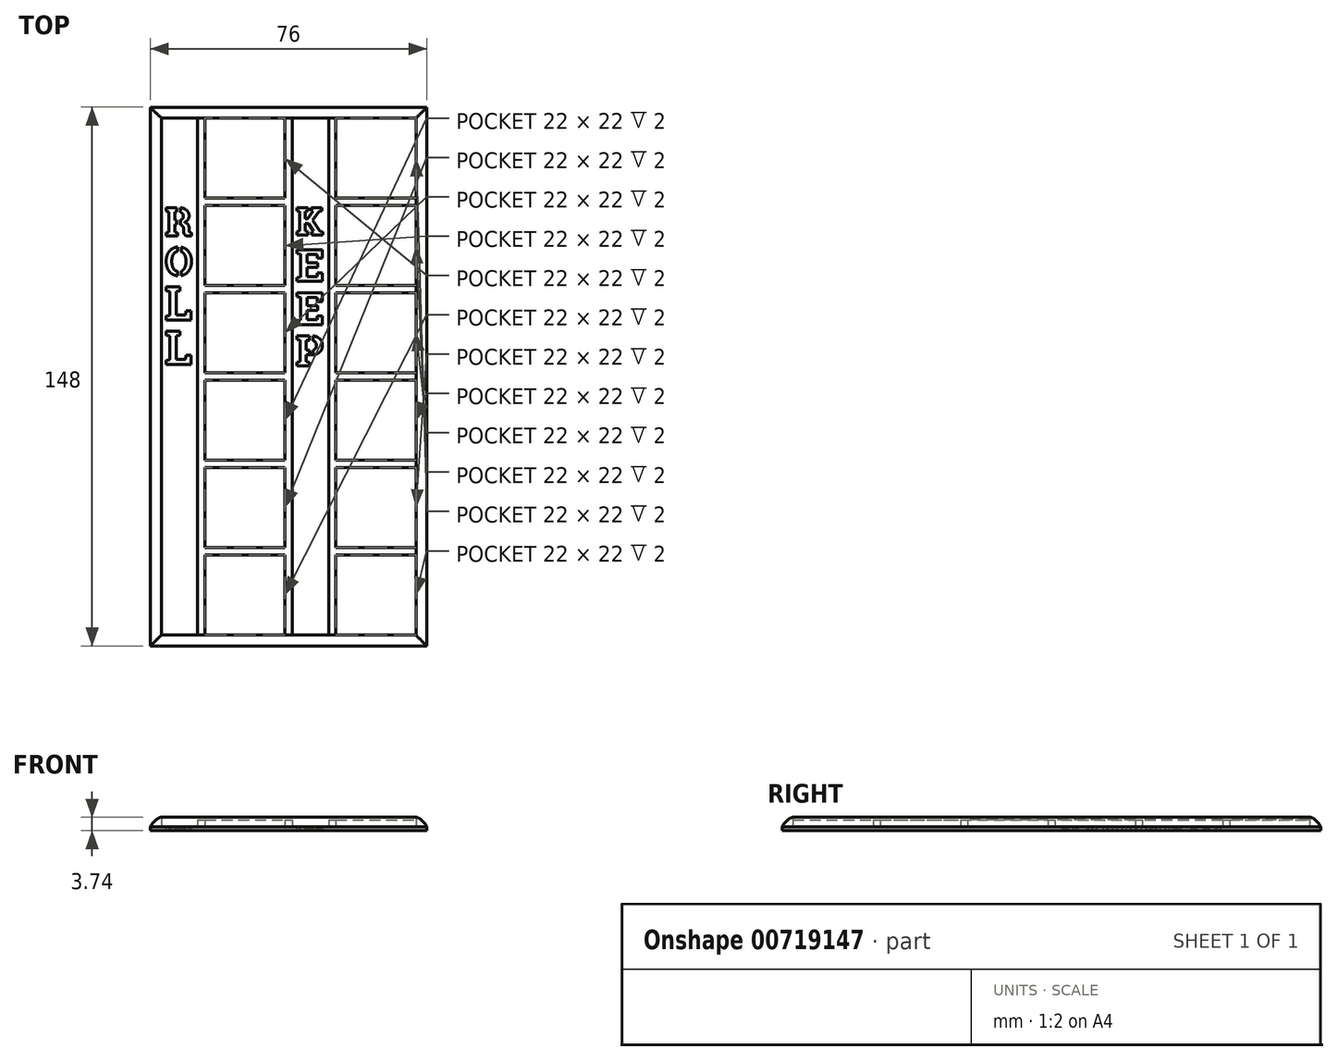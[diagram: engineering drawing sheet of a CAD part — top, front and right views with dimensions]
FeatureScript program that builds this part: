
annotation { "Feature Type Name" : "Feature", "Feature Type Description" : "" }
export const myFeature = defineFeature(function(context is Context, id is Id, definition is map)
    precondition{}
    {
        {
            var Q0;
            Q0=qCreatedBy(makeId("Top.planeOp"),FACE);
            var sketch = newSketch(context, id + "F0", { "sketchPlane" : qUnion([Q0])});
            skLineSegment(sketch, "E0.bottom", {"start": v(-38, 75.1) * mm, "end": v(38, 75.1) * mm});
            skLineSegment(sketch, "E0.top", {"start": v(-38, -72.9) * mm, "end": v(38, -72.9) * mm});
            skLineSegment(sketch, "E0.left", {"start": v(-38, 75.1) * mm, "end": v(-38, -72.9) * mm});
            skLineSegment(sketch, "E0.right", {"start": v(38, 75.1) * mm, "end": v(38, -72.9) * mm});
            skLineSegment(sketch, "E1.left", {"start": v(11, -69.9) * mm, "end": v(11, 72.1) * mm});
            skLineSegment(sketch, "E1.right", {"start": v(-35, -69.9) * mm, "end": v(-35, 72.1) * mm});
            skLineSegment(sketch, "E2", {"start": v(-25, 72.1) * mm, "end": v(-25, -69.9) * mm});
            skLineSegment(sketch, "E3.1.0.0", {"start": v(-1, 72.1) * mm, "end": v(-1, -69.9) * mm});
            skLineSegment(sketch, "E3.2.0.0", {"start": v(13, 72.1) * mm, "end": v(13, -69.9) * mm});
            skLineSegment(sketch, "E4", {"start": v(-23, -69.9) * mm, "end": v(-23, 72.1) * mm});
            skLineSegment(sketch, "E5.1.0.0", {"start": v(1, -69.9) * mm, "end": v(1, 72.1) * mm});
            skLineSegment(sketch, "E5.2.0.0", {"start": v(35, -69.9) * mm, "end": v(35, 72.1) * mm});
            skLineSegment(sketch, "E6", {"start": v(-35, 72.1) * mm, "end": v(35, 72.1) * mm});
            skLineSegment(sketch, "E7", {"start": v(35, -69.9) * mm, "end": v(-35, -69.9) * mm});
            skLineSegment(sketch, "E8.bottom", {"start": v(-29.5, 28.1) * mm, "end": v(-30.5, 28.1) * mm});
            skLineSegment(sketch, "E8.top", {"start": v(-29.5, 38.1) * mm, "end": v(-30.5, 38.1) * mm});
            skLineSegment(sketch, "E8.left", {"start": v(-29.5, 28.1) * mm, "end": v(-29.5, 38.1) * mm});
            skLineSegment(sketch, "E8.right", {"start": v(-30.5, 28.1) * mm, "end": v(-30.5, 38.1) * mm});
            skLineSegment(sketch, "E9.bottom", {"start": v(-30.75, 48.1) * mm, "end": v(-29.75, 48.1) * mm});
            skLineSegment(sketch, "E9.top", {"start": v(-30.75, 42.1) * mm, "end": v(-29.75, 42.1) * mm});
            skLineSegment(sketch, "E9.left", {"start": v(-30.75, 48.1) * mm, "end": v(-30.75, 42.1) * mm});
            skLineSegment(sketch, "E9.right", {"start": v(-29.75, 48.1) * mm, "end": v(-29.75, 42.1) * mm});
            skLineSegment(sketch, "E10.bottom", {"start": v(5.75, 7.6) * mm, "end": v(6.75, 7.6) * mm});
            skLineSegment(sketch, "E10.top", {"start": v(5.75, 13.6) * mm, "end": v(6.75, 13.6) * mm});
            skLineSegment(sketch, "E10.left", {"start": v(5.75, 7.6) * mm, "end": v(5.75, 13.6) * mm});
            skLineSegment(sketch, "E10.right", {"start": v(6.75, 7.6) * mm, "end": v(6.75, 13.6) * mm});
            skSolve(sketch);
        }
        {
            var Q0;
            Q0=qCreatedBy(makeId("Top.planeOp"),FACE);
            var sketch = newSketch(context, id + "F1", { "sketchPlane" : qUnion([Q0])});
            skLineSegment(sketch, "E11", {"start": v(-25, 72.1) * mm, "end": v(-25, -69.9) * mm});
            skLineSegment(sketch, "E12", {"start": v(-35, -69.9) * mm, "end": v(-35, 72.1) * mm});
            skLineSegment(sketch, "E13", {"start": v(11, -69.9) * mm, "end": v(11, 72.1) * mm});
            skLineSegment(sketch, "E14", {"start": v(13, 72.1) * mm, "end": v(13, -69.9) * mm});
            skLineSegment(sketch, "E15", {"start": v(-23, 72.1) * mm, "end": v(-1, 72.1) * mm});
            skLineSegment(sketch, "E16", {"start": v(-23, -69.9) * mm, "end": v(-23, 72.1) * mm});
            skLineSegment(sketch, "E17", {"start": v(-1, -69.9) * mm, "end": v(-23, -69.9) * mm});
            skLineSegment(sketch, "E18", {"start": v(-1, 72.1) * mm, "end": v(-1, -69.9) * mm});
            skLineSegment(sketch, "E19", {"start": v(-25, 72.1) * mm, "end": v(-23, 72.1) * mm});
            skLineSegment(sketch, "E20", {"start": v(-23, -69.9) * mm, "end": v(-25, -69.9) * mm});
            skLineSegment(sketch, "E21.bottom", {"start": v(-23, 50.1) * mm, "end": v(-1, 50.1) * mm});
            skLineSegment(sketch, "E21.top", {"start": v(-23, 48.1) * mm, "end": v(-1, 48.1) * mm});
            skLineSegment(sketch, "E21.left", {"start": v(-23, 50.1) * mm, "end": v(-23, 48.1) * mm});
            skLineSegment(sketch, "E21.right", {"start": v(-1, 50.1) * mm, "end": v(-1, 48.1) * mm});
            skLineSegment(sketch, "E22.bottom", {"start": v(-23, 26.1) * mm, "end": v(-1, 26.1) * mm});
            skLineSegment(sketch, "E22.top", {"start": v(-23, 24.1) * mm, "end": v(-1, 24.1) * mm});
            skLineSegment(sketch, "E23.bottom", {"start": v(-23, 2.1) * mm, "end": v(-1, 2.1) * mm});
            skLineSegment(sketch, "E23.top", {"start": v(-23, 0.1) * mm, "end": v(-1, 0.1) * mm});
            skLineSegment(sketch, "E24.bottom", {"start": v(-23, -21.9) * mm, "end": v(-1, -21.9) * mm});
            skLineSegment(sketch, "E24.top", {"start": v(-23, -23.9) * mm, "end": v(-1, -23.9) * mm});
            skLineSegment(sketch, "E25.bottom", {"start": v(-23, -45.9) * mm, "end": v(-1, -45.9) * mm});
            skLineSegment(sketch, "E25.top", {"start": v(-23, -47.9) * mm, "end": v(-1, -47.9) * mm});
            skLineSegment(sketch, "E26.bottom", {"start": v(13, 50.1) * mm, "end": v(35, 50.1) * mm});
            skLineSegment(sketch, "E26.top", {"start": v(13, 48.1) * mm, "end": v(35, 48.1) * mm});
            skLineSegment(sketch, "E27.bottom", {"start": v(13, 26.1) * mm, "end": v(35, 26.1) * mm});
            skLineSegment(sketch, "E27.top", {"start": v(13, 24.1) * mm, "end": v(35, 24.1) * mm});
            skLineSegment(sketch, "E28.bottom", {"start": v(13, 2.1) * mm, "end": v(35, 2.1) * mm});
            skLineSegment(sketch, "E28.top", {"start": v(13, 0.1) * mm, "end": v(35, 0.1) * mm});
            skLineSegment(sketch, "E29.bottom", {"start": v(13, -21.9) * mm, "end": v(35, -21.9) * mm});
            skLineSegment(sketch, "E29.top", {"start": v(13, -23.9) * mm, "end": v(35, -23.9) * mm});
            skLineSegment(sketch, "E30.bottom", {"start": v(13, -45.9) * mm, "end": v(35, -45.9) * mm});
            skLineSegment(sketch, "E30.top", {"start": v(13, -47.9) * mm, "end": v(35, -47.9) * mm});
            skLineSegment(sketch, "E31", {"start": v(13, -69.9) * mm, "end": v(11, -69.9) * mm});
            skLineSegment(sketch, "E32", {"start": v(11, 72.1) * mm, "end": v(13, 72.1) * mm});
            skLineSegment(sketch, "E33", {"start": v(35, -69.9) * mm, "end": v(13, -69.9) * mm});
            skLineSegment(sketch, "E34", {"start": v(35, -69.9) * mm, "end": v(35, 72.1) * mm});
            skLineSegment(sketch, "E35", {"start": v(13, 72.1) * mm, "end": v(35, 72.1) * mm});
            skSolve(sketch);
        }
        {
            var Q0;
            Q0=makeQuery(id+"F0.imprint","IMPRINT",FACE,{"disambiguationData":[TD([[makeQuery(id+"F0.imprint","IMPRINT",EDGE,{"derivedFrom":sQuery(id+"F0.wireOp",EDGE,"E0.bottom")}),-1.0]])]});
            var Q1;
            Q1=sQuery(id+"F0.wireOp",EDGE,"E1.top");
            var Q2;
            Q2=sQuery(id+"F1.wireOp",EDGE,"1024a238-9103-462a-9477-26902ec0aa7303");
            var Q3;
            Q3=sQuery(id+"F0.wireOp",EDGE,"E0.bottom");
            var Q4;
            Q4=sQuery(id+"F0.wireOp",EDGE,"E1.right");
            var Q5;
            Q5=sQuery(id+"F0.wireOp",EDGE,"E0.left");
            var Q6;
            Q6=sQuery(id+"F0.wireOp",EDGE,"E0.top");
            var Q7;
            Q7=sQuery(id+"F0.wireOp",EDGE,"E1.bottom");
            var Q8;
            Q8=sQuery(id+"F1.wireOp",EDGE,"1024a238-9103-462a-9477-26902ec0aa7301");
            var Q9;
            Q9=sQuery(id+"F0.wireOp",EDGE,"E1.left");
            var Q10;
            Q10=sQuery(id+"F0.wireOp",EDGE,"E0.right");
            extrude(context, id + "F2", {"entities" : qUnion([Q0]), "surfaceEntities" : qUnion([Q1, Q2, Q3, Q4, Q5, Q6, Q7, Q8, Q9, Q10]), "depth" : 3 * mm, "offsetDistance" : 25 * mm});
        }
        {
            var Q0;
            {var subQ0=sQuery(id+"F0.wireOp",EDGE,"E2");Q0=makeQuery(id+"F0.imprint","IMPRINT",FACE,{"disambiguationData":[TD([[makeQuery(id+"F0.imprint","IMPRINT",EDGE,{"derivedFrom":subQ0}),1.0]])]});}
            var Q1;
            {var subQ0=sQuery(id+"F0.wireOp",EDGE,"E3.1.0.0");Q1=makeQuery(id+"F0.imprint","IMPRINT",FACE,{"disambiguationData":[TD([[makeQuery(id+"F0.imprint","IMPRINT",EDGE,{"derivedFrom":subQ0}),1.0]])]});}
            var Q2;
            {var subQ0=sQuery(id+"F0.wireOp",EDGE,"E1.left");Q2=makeQuery(id+"F0.imprint","IMPRINT",FACE,{"disambiguationData":[TD([[makeQuery(id+"F0.imprint","IMPRINT",EDGE,{"derivedFrom":subQ0}),-1.0]])]});}
            var Q3;
            Q3=sQuery(id+"F0.wireOp",EDGE,"E2");
            var Q4;
            Q4=sQuery(id+"F0.wireOp",EDGE,"E4");
            extrude(context, id + "F3", {"entities" : qUnion([Q0, Q1, Q2]), "operationType" : NewBodyOperationType.ADD, "surfaceEntities" : qUnion([Q3, Q4]), "depth" : 2 * mm, "offsetDistance" : 25 * mm});
        }
        {
            var Q0;
            Q0=makeQuery(id+"F2.opExtrude","CAP_EDGE",EDGE,{"disambiguationData":[OSD([sQuery(id+"F0.wireOp",EDGE,"E0.right")])],"isStart":false});
            var Q1;
            Q1=makeQuery(id+"F2.opExtrude","CAP_EDGE",EDGE,{"disambiguationData":[OSD([sQuery(id+"F0.wireOp",EDGE,"E0.top")])],"isStart":false});
            var Q2;
            Q2=makeQuery(id+"F2.opExtrude","CAP_EDGE",EDGE,{"disambiguationData":[OSD([sQuery(id+"F0.wireOp",EDGE,"E0.left")])],"isStart":false});
            var Q3;
            Q3=makeQuery(id+"F2.opExtrude","CAP_EDGE",EDGE,{"disambiguationData":[OSD([sQuery(id+"F0.wireOp",EDGE,"E0.bottom")])],"isStart":false});
            fillet(context, id + "F4", {"entities" : qUnion([Q0, Q1, Q2, Q3]), "radius" : 5 * mm, "tangentPropagation" : true, "allowEdgeOverflow" : false});
        }
        {
            var Q0;
            Q0=qCreatedBy(makeId("Top.planeOp"),FACE);
            var sketch = newSketch(context, id + "F5", { "sketchPlane" : qUnion([Q0])});
            skLineSegment(sketch, "E36.bottom", {"start": v(-38, -72.9) * mm, "end": v(38, -72.9) * mm});
            skLineSegment(sketch, "E36.top", {"start": v(-38, 75.1) * mm, "end": v(38, 75.1) * mm});
            skLineSegment(sketch, "E36.left", {"start": v(-38, -72.9) * mm, "end": v(-38, 75.1) * mm});
            skLineSegment(sketch, "E36.right", {"start": v(38, -72.9) * mm, "end": v(38, 75.1) * mm});
            skSolve(sketch);
        }
        {
            var Q0;
            {var subQ0=sQuery(id+"F1.wireOp",EDGE,"E26.bottom");Q0=makeQuery(id+"F1.imprint","IMPRINT",FACE,{"disambiguationData":[TD([[makeQuery(id+"F1.imprint","IMPRINT",EDGE,{"derivedFrom":subQ0}),-1.0]])]});}
            var Q1;
            {var subQ0=sQuery(id+"F1.wireOp",EDGE,"E27.bottom");Q1=makeQuery(id+"F1.imprint","IMPRINT",FACE,{"disambiguationData":[TD([[makeQuery(id+"F1.imprint","IMPRINT",EDGE,{"derivedFrom":subQ0}),-1.0]])]});}
            var Q2;
            {var subQ0=sQuery(id+"F1.wireOp",EDGE,"E28.bottom");Q2=makeQuery(id+"F1.imprint","IMPRINT",FACE,{"disambiguationData":[TD([[makeQuery(id+"F1.imprint","IMPRINT",EDGE,{"derivedFrom":subQ0}),-1.0]])]});}
            var Q3;
            {var subQ0=sQuery(id+"F1.wireOp",EDGE,"E29.bottom");Q3=makeQuery(id+"F1.imprint","IMPRINT",FACE,{"disambiguationData":[TD([[makeQuery(id+"F1.imprint","IMPRINT",EDGE,{"derivedFrom":subQ0}),-1.0]])]});}
            var Q4;
            {var subQ0=sQuery(id+"F1.wireOp",EDGE,"E30.bottom");Q4=makeQuery(id+"F1.imprint","IMPRINT",FACE,{"disambiguationData":[TD([[makeQuery(id+"F1.imprint","IMPRINT",EDGE,{"derivedFrom":subQ0}),-1.0]])]});}
            var Q5;
            {var subQ0=sQuery(id+"F1.wireOp",EDGE,"E25.bottom");Q5=makeQuery(id+"F1.imprint","IMPRINT",FACE,{"disambiguationData":[TD([[makeQuery(id+"F1.imprint","IMPRINT",EDGE,{"derivedFrom":subQ0}),-1.0]])]});}
            var Q6;
            {var subQ0=sQuery(id+"F1.wireOp",EDGE,"E24.bottom");Q6=makeQuery(id+"F1.imprint","IMPRINT",FACE,{"disambiguationData":[TD([[makeQuery(id+"F1.imprint","IMPRINT",EDGE,{"derivedFrom":subQ0}),-1.0]])]});}
            var Q7;
            {var subQ0=sQuery(id+"F1.wireOp",EDGE,"E23.bottom");Q7=makeQuery(id+"F1.imprint","IMPRINT",FACE,{"disambiguationData":[TD([[makeQuery(id+"F1.imprint","IMPRINT",EDGE,{"derivedFrom":subQ0}),-1.0]])]});}
            var Q8;
            {var subQ0=sQuery(id+"F1.wireOp",EDGE,"E22.bottom");Q8=makeQuery(id+"F1.imprint","IMPRINT",FACE,{"disambiguationData":[TD([[makeQuery(id+"F1.imprint","IMPRINT",EDGE,{"derivedFrom":subQ0}),-1.0]])]});}
            var Q9;
            Q9=makeQuery(id+"F1.imprint","IMPRINT",FACE,{"disambiguationData":[TD([[makeQuery(id+"F1.imprint","IMPRINT",EDGE,{"derivedFrom":sQuery(id+"F1.wireOp",EDGE,"E21.bottom")}),-1.0]])]});
            extrude(context, id + "F6", {"entities" : qUnion([Q0, Q1, Q2, Q3, Q4, Q5, Q6, Q7, Q8, Q9]), "operationType" : NewBodyOperationType.ADD, "depth" : 2 * mm, "offsetDistance" : 25 * mm});
        }
        {
            var Q0;
            Q0=qCreatedBy(makeId("Top.planeOp"),FACE);
            var sketch = newSketch(context, id + "F7", { "sketchPlane" : qUnion([Q0])});
            skText(sketch, "E37", { "text": "R", "fontName": "RobotoSlab-Bold.ttf"});
            const initialGuessF7  = {"E37": [-0.034, 0.0397, 1, 0, 0.0079]};
            skSetInitialGuess(sketch, initialGuessF7);
            skSolve(sketch);
        }
        {
            var Q0;
            Q0=qCreatedBy(makeId("Top.planeOp"),FACE);
            var sketch = newSketch(context, id + "F8", { "sketchPlane" : qUnion([Q0])});
            skText(sketch, "E38", { "text": "O", "fontName": "RobotoSlab-Bold.ttf"});
            const initialGuessF8  = {"E38": [-0.034, 0.0289, 1, 0, 0.0078], "E38": [-0.034, 0.0289, 1, 0, 0.0078]};
            skSetInitialGuess(sketch, initialGuessF8);
            skSolve(sketch);
        }
        {
            var Q0;
            Q0=qCreatedBy(makeId("Top.planeOp"),FACE);
            var sketch = newSketch(context, id + "F9", { "sketchPlane" : qUnion([Q0])});
            skText(sketch, "E39", { "text": "L", "fontName": "RobotoSlab-Bold.ttf"});
            const initialGuessF9  = {"E39": [-0.034, 0.01666, 1, 0, 0.00924]};
            skSetInitialGuess(sketch, initialGuessF9);
            skSolve(sketch);
        }
        {
            var Q0;
            Q0=qCreatedBy(makeId("Top.planeOp"),FACE);
            var sketch = newSketch(context, id + "F10", { "sketchPlane" : qUnion([Q0])});
            skText(sketch, "E40", { "text": "L", "fontName": "RobotoSlab-Bold.ttf"});
            const initialGuessF10  = {"E40": [-0.034, 0.00442, 1, 0, 0.00924]};
            skSetInitialGuess(sketch, initialGuessF10);
            skSolve(sketch);
        }
        {
            var Q0;
            Q0=qCreatedBy(makeId("Top.planeOp"),FACE);
            var sketch = newSketch(context, id + "F11", { "sketchPlane" : qUnion([Q0])});
            skText(sketch, "E41", { "text": "K", "fontName": "RobotoSlab-Bold.ttf"});
            const initialGuessF11  = {"E41": [0.002, 0.04004, 1, 0, 0.00757]};
            skSetInitialGuess(sketch, initialGuessF11);
            skSolve(sketch);
        }
        {
            var Q0;
            Q0=qCreatedBy(makeId("Top.planeOp"),FACE);
            var sketch = newSketch(context, id + "F12", { "sketchPlane" : qUnion([Q0])});
            skText(sketch, "E42", { "text": "E", "fontName": "RobotoSlab-Bold.ttf"});
            const initialGuessF12  = {"E42": [0.002, 0.02724, 1, 0, 0.00885]};
            skSetInitialGuess(sketch, initialGuessF12);
            skSolve(sketch);
        }
        {
            var Q0;
            Q0=qCreatedBy(makeId("Top.planeOp"),FACE);
            var sketch = newSketch(context, id + "F13", { "sketchPlane" : qUnion([Q0])});
            skText(sketch, "E43", { "text": "E", "fontName": "RobotoSlab-Bold.ttf"});
            const initialGuessF13  = {"E43": [0.002, 0.0154, 1, 0, 0.00885]};
            skSetInitialGuess(sketch, initialGuessF13);
            skSolve(sketch);
        }
        {
            var Q0;
            Q0=qCreatedBy(makeId("Top.planeOp"),FACE);
            var sketch = newSketch(context, id + "F14", { "sketchPlane" : qUnion([Q0])});
            skText(sketch, "E44", { "text": "P", "fontName": "RobotoSlab-Bold.ttf"});
            const initialGuessF14  = {"E44": [0.002, 0.00405, 1, 0, 0.00835]};
            skSetInitialGuess(sketch, initialGuessF14);
            skSolve(sketch);
        }
        {
            var Q0;
            Q0=qSketchRegion(id+"F5",true);
            extrude(context, id + "F15", {"entities" : qUnion([Q0]), "operationType" : NewBodyOperationType.ADD, "oppositeDirection" : true, "depth" : 1 * mm, "offsetDistance" : 25 * mm});
        }
        {
            var Q0;
            Q0=qSketchRegion(id+"F14",true);
            var Q1;
            Q1=qSketchRegion(id+"F11",true);
            var Q2;
            Q2=qSketchRegion(id+"F12",true);
            var Q3;
            Q3=qSketchRegion(id+"F9",true);
            var Q4;
            Q4=qSketchRegion(id+"F10",true);
            var Q5;
            Q5=qSketchRegion(id+"F7",true);
            var Q6;
            Q6=qSketchRegion(id+"F8",true);
            var Q7;
            Q7=qSketchRegion(id+"F13",true);
            extrude(context, id + "F16", {"entities" : qUnion([Q0, Q1, Q2, Q3, Q4, Q5, Q6, Q7]), "operationType" : NewBodyOperationType.REMOVE, "oppositeDirection" : true, "depth" : 10 * mm, "offsetDistance" : 25 * mm});
        }
        {
            var Q0;
            Q0=makeQuery(id+"F0.imprint","IMPRINT",FACE,{"disambiguationData":[TD([[makeQuery(id+"F0.imprint","IMPRINT",EDGE,{"derivedFrom":sQuery(id+"F0.wireOp",EDGE,"E8.bottom")}),-1.0]])]});
            extrude(context, id + "F17", {"entities" : qUnion([Q0]), "operationType" : NewBodyOperationType.ADD, "oppositeDirection" : true, "depth" : 1 * mm, "offsetDistance" : 25 * mm});
        }
        {
            var Q0;
            Q0=makeQuery(id+"F0.imprint","IMPRINT",FACE,{"disambiguationData":[TD([[makeQuery(id+"F0.imprint","IMPRINT",EDGE,{"derivedFrom":sQuery(id+"F0.wireOp",EDGE,"E9.bottom")}),-1.0]])]});
            extrude(context, id + "F18", {"entities" : qUnion([Q0]), "operationType" : NewBodyOperationType.ADD, "oppositeDirection" : true, "depth" : 1 * mm, "offsetDistance" : 25 * mm});
        }
        {
            var Q0;
            Q0=makeQuery(id+"F0.imprint","IMPRINT",FACE,{"disambiguationData":[TD([[makeQuery(id+"F0.imprint","IMPRINT",EDGE,{"derivedFrom":sQuery(id+"F0.wireOp",EDGE,"E10.bottom")}),1.0]])]});
            extrude(context, id + "F19", {"entities" : qUnion([Q0]), "operationType" : NewBodyOperationType.ADD, "oppositeDirection" : true, "depth" : 1 * mm, "offsetDistance" : 25 * mm});
        }
    });
